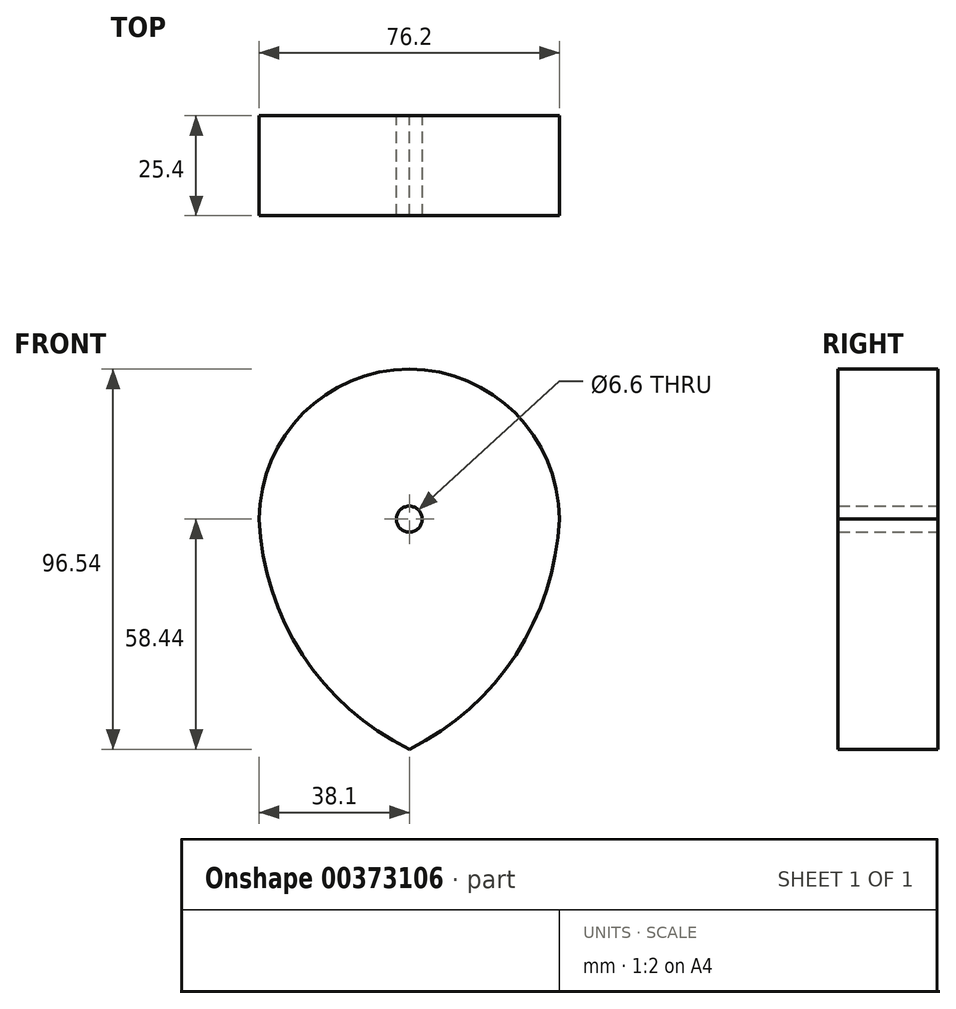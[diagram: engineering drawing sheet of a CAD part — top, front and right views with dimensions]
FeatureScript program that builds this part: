
annotation { "Feature Type Name" : "Feature", "Feature Type Description" : "" }
export const myFeature = defineFeature(function(context is Context, id is Id, definition is map)
    precondition{}
    {
        {
            var Q0;
            Q0=qCreatedBy(makeId("Front.planeOp"),FACE);
            var sketch = newSketch(context, id + "F0", { "sketchPlane" : qUnion([Q0])});
            skArc(sketch, "E0", {"start": v(38.1, 0) * mm, "mid": v(0, 38.1) * mm, "end": v(-38.1, 0) * mm});
            skArc(sketch, "E1", {"start": v(0, -58.44) * mm, "mid": v(27.06, -34.44) * mm, "end": v(38.1, 0) * mm});
            skArc(sketch, "E2", {"start": v(-38.1, 0) * mm, "mid": v(-27.12, -34.48) * mm, "end": v(0, -58.44) * mm});
            skSolve(sketch);
        }
        {
            var Q0;
            Q0=sQuery(id+"F0.wireOp",EDGE,"E1");
            extrude(context, id + "F1", {"bodyType" : ToolBodyType.SURFACE, "surfaceEntities" : qUnion([Q0]), "depth" : 25.4 * mm});
        }
        {
            var Q0;
            Q0 = qSketchRegion(id + "F0", true);
            extrude(context, id + "F2", {"entities" : qUnion([Q0]), "depth" : 25.4 * mm});
        }
        {
            var Q0;
            Q0=makeQuery(id+"F2.opExtrude","CAP_FACE",FACE,{"disambiguationData":[OSD([sQuery(id+"F0.wireOp",EDGE,"E0"),sQuery(id+"F0.wireOp",EDGE,"E1"),sQuery(id+"F0.wireOp",EDGE,"E2")])],"isStart":true});
            var sketch = newSketch(context, id + "F3", { "sketchPlane" : qUnion([Q0])});
            skCircle(sketch, "E3", {"center": v(0, 0) * mm, "radius": 3.3 * mm});
            skSolve(sketch);
        }
        {
            var Q0;
            Q0 = qSketchRegion(id + "F3", true);
            extrude(context, id + "F4", {"entities" : qUnion([Q0]), "operationType" : NewBodyOperationType.REMOVE, "oppositeDirection" : true, "depth" : 25.4 * mm});
        }
    });
